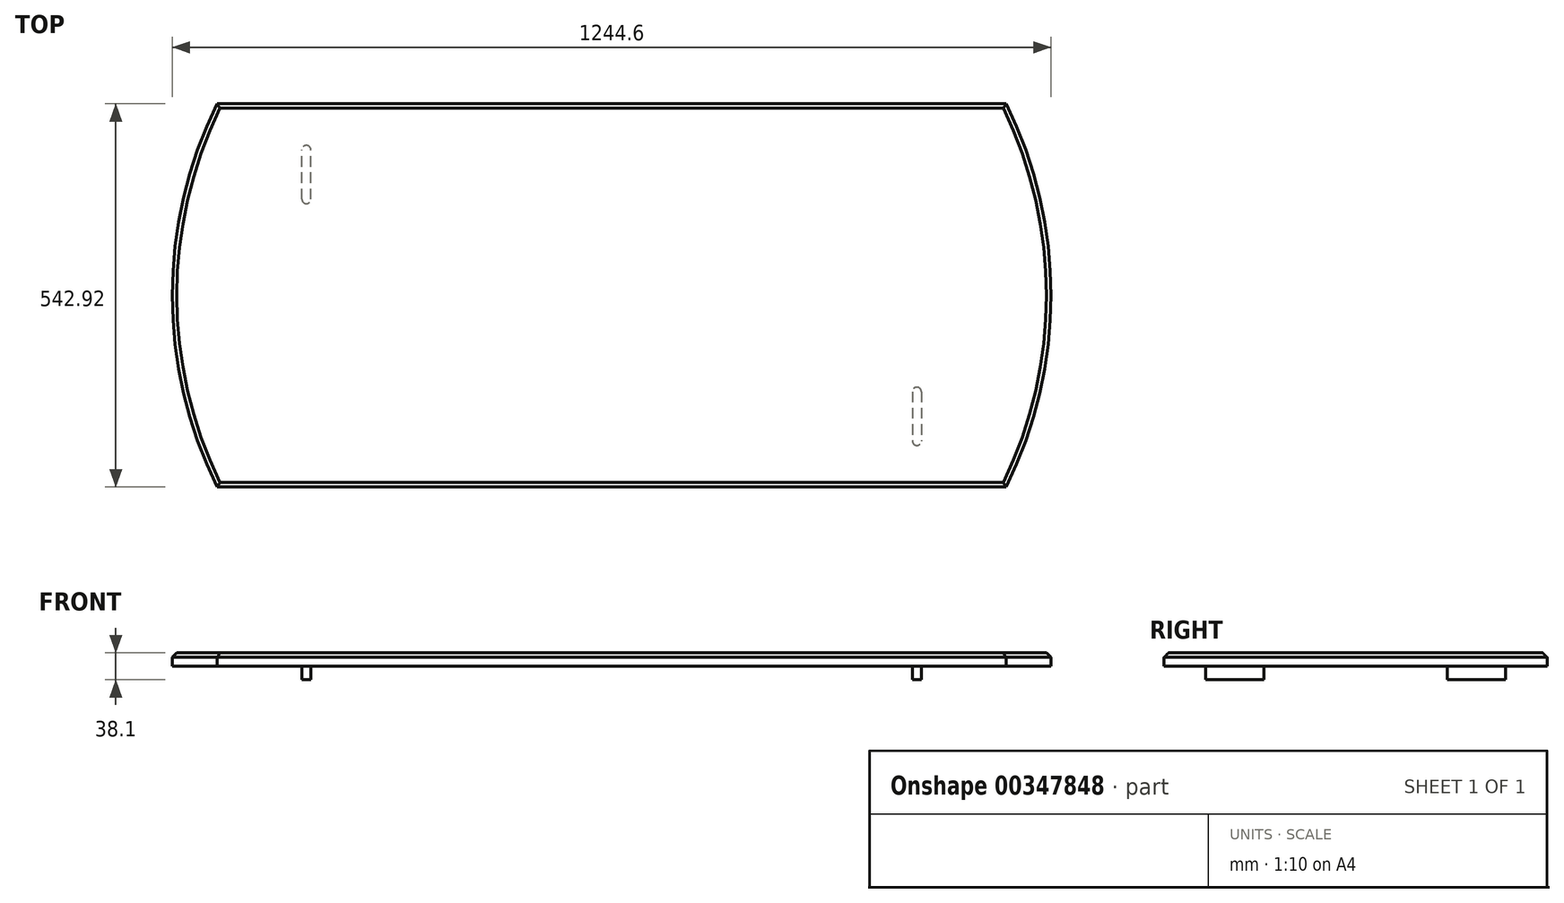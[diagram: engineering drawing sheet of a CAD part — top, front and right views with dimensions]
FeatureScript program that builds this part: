
annotation { "Feature Type Name" : "Feature", "Feature Type Description" : "" }
export const myFeature = defineFeature(function(context is Context, id is Id, definition is map)
    precondition{}
    {
        {
            var Q0;
            Q0=qCreatedBy(makeId("Front.planeOp"),FACE);
            var sketch = newSketch(context, id + "F0", { "sketchPlane" : qUnion([Q0])});
            skLineSegment(sketch, "E0.bottom", {"start": v(-622.3, -19.05) * mm, "end": v(622.3, -19.05) * mm});
            skLineSegment(sketch, "E0.top", {"start": v(-622.3, 19.05) * mm, "end": v(622.3, 19.05) * mm});
            skLineSegment(sketch, "E0.left", {"start": v(-622.3, -19.05) * mm, "end": v(-622.3, 19.05) * mm});
            skLineSegment(sketch, "E0.right", {"start": v(622.3, -19.05) * mm, "end": v(622.3, 19.05) * mm});
            skPoint(sketch, "E0.middle", {"position": v(0, 0) * mm});
            skSolve(sketch);
        }
        {
            var Q0;
            Q0=makeQuery(id+"F0.imprint","IMPRINT",FACE,{"disambiguationData":[TD([[makeQuery(id+"F0.imprint","IMPRINT",EDGE,{"derivedFrom":sQuery(id+"F0.wireOp",EDGE,"E0.bottom")}),1.0]])]});
            extrude(context, id + "F1", {"entities" : qUnion([Q0]), "endBound" : BoundingType.SYMMETRIC, "depth" : 542.92 * mm});
        }
        {
            var Q0;
            Q0=makeQuery(id+"F1.opExtrude","SWEPT_FACE",FACE,{"disambiguationData":[OSD([sQuery(id+"F0.wireOp",EDGE,"E0.top")])]});
            var sketch = newSketch(context, id + "F2", { "sketchPlane" : qUnion([Q0])});
            skLineSegment(sketch, "E1", {"start": v(-622.3, 0) * mm, "end": v(622.3, 0) * mm, "construction": true});
            skLineSegment(sketch, "E2", {"start": v(0, 271.46) * mm, "end": v(0, -271.46) * mm, "construction": true});
            skPoint(sketch, "E3", {"position": v(-558.8, 271.46) * mm});
            skPoint(sketch, "E4.MirrorP", {"position": v(-558.8, -271.46) * mm});
            skPoint(sketch, "E5.MirrorP", {"position": v(558.8, 271.46) * mm});
            skPoint(sketch, "E6.MirrorP", {"position": v(558.8, -271.46) * mm});
            skArc(sketch, "E7", {"start": v(-558.8, 271.46) * mm, "mid": v(-622.3, 0) * mm, "end": v(-558.8, -271.46) * mm});
            skArc(sketch, "E8", {"start": v(558.8, -271.46) * mm, "mid": v(622.3, 0) * mm, "end": v(558.8, 271.46) * mm});
            skSolve(sketch);
        }
        {
            var Q0;
            {var subQ0=sQuery(id+"F2.wireOp",EDGE,"E7");var subQ1=sQuery(id+"F0.wireOp",EDGE,"E0.top");var subQ2=makeQuery(id+"F1.opExtrude","CAP_EDGE",EDGE,{"disambiguationData":[OSD([subQ1])],"isStart":true});var subQ3=makeQuery(id+"F2.imprint","INTERSECT",VERTEX,{"derivedFrom":[subQ2,subQ0]});Q0=makeQuery(id+"F2.imprint","IMPRINT",FACE,{"disambiguationData":[TD([[makeQuery(id+"F2.imprint","IMPRINT",EDGE,{"disambiguationData":[TD([[subQ3,-1.0]])],"derivedFrom":subQ0}),-1.0]])]});}
            var Q1;
            {var subQ0=sQuery(id+"F2.wireOp",EDGE,"E7");var subQ1=sQuery(id+"F0.wireOp",EDGE,"E0.top");var subQ2=makeQuery(id+"F1.opExtrude","CAP_EDGE",EDGE,{"disambiguationData":[OSD([subQ1])],"isStart":false});var subQ3=makeQuery(id+"F2.imprint","INTERSECT",VERTEX,{"derivedFrom":[subQ2,subQ0]});Q1=makeQuery(id+"F2.imprint","IMPRINT",FACE,{"disambiguationData":[TD([[makeQuery(id+"F2.imprint","IMPRINT",EDGE,{"disambiguationData":[TD([[subQ3,1.0]])],"derivedFrom":subQ0}),-1.0]])]});}
            var Q2;
            {var subQ0=sQuery(id+"F2.wireOp",EDGE,"E8");var subQ1=sQuery(id+"F0.wireOp",EDGE,"E0.top");var subQ2=makeQuery(id+"F1.opExtrude","CAP_EDGE",EDGE,{"disambiguationData":[OSD([subQ1])],"isStart":true});var subQ3=makeQuery(id+"F2.imprint","INTERSECT",VERTEX,{"derivedFrom":[subQ2,subQ0]});Q2=makeQuery(id+"F2.imprint","IMPRINT",FACE,{"disambiguationData":[TD([[makeQuery(id+"F2.imprint","IMPRINT",EDGE,{"disambiguationData":[TD([[subQ3,1.0]])],"derivedFrom":subQ0}),-1.0]])]});}
            var Q3;
            {var subQ0=sQuery(id+"F2.wireOp",EDGE,"E8");var subQ1=sQuery(id+"F0.wireOp",EDGE,"E0.top");var subQ2=makeQuery(id+"F1.opExtrude","CAP_EDGE",EDGE,{"disambiguationData":[OSD([subQ1])],"isStart":false});var subQ3=makeQuery(id+"F2.imprint","INTERSECT",VERTEX,{"derivedFrom":[subQ2,subQ0]});Q3=makeQuery(id+"F2.imprint","IMPRINT",FACE,{"disambiguationData":[TD([[makeQuery(id+"F2.imprint","IMPRINT",EDGE,{"disambiguationData":[TD([[subQ3,-1.0]])],"derivedFrom":subQ0}),-1.0]])]});}
            extrude(context, id + "F3", {"entities" : qUnion([Q0, Q1, Q2, Q3]), "operationType" : NewBodyOperationType.REMOVE, "endBound" : BoundingType.THROUGH_ALL, "oppositeDirection" : true, "depth" : 25.4 * mm});
        }
        {
            var Q0;
            Q0=makeQuery(id+"F1.opExtrude","SWEPT_FACE",FACE,{"disambiguationData":[OSD([sQuery(id+"F0.wireOp",EDGE,"E0.top")])]});
            chamfer(context, id + "F4", {"entities" : qUnion([Q0]), "width" : 6.35 * mm, "tangentPropagation" : true});
        }
        {
            var Q0;
            Q0=makeQuery(id+"F1.opExtrude","SWEPT_FACE",FACE,{"disambiguationData":[OSD([sQuery(id+"F0.wireOp",EDGE,"E0.bottom")])]});
            var sketch = newSketch(context, id + "F5", { "sketchPlane" : qUnion([Q0])});
            skArc(sketch, "E9.0", {"start": v(-554.84, 265.11) * mm, "mid": v(-615.95, 0) * mm, "end": v(-554.84, -265.11) * mm});
            skLineSegment(sketch, "E9.1", {"start": v(554.84, 265.11) * mm, "end": v(-554.84, 265.11) * mm});
            skArc(sketch, "E9.2", {"start": v(554.84, -265.11) * mm, "mid": v(615.95, 0) * mm, "end": v(554.84, 265.11) * mm});
            skLineSegment(sketch, "E9.3", {"start": v(-554.84, -265.11) * mm, "end": v(554.84, -265.11) * mm});
            skSolve(sketch);
        }
        {
            var Q0;
            Q0=makeQuery(id+"F5.imprint","IMPRINT",FACE,{"disambiguationData":[TD([[makeQuery(id+"F5.imprint","IMPRINT",EDGE,{"derivedFrom":sQuery(id+"F5.wireOp",EDGE,"E9.0")}),-1.0]])]});
            extrude(context, id + "F6", {"entities" : qUnion([Q0]), "operationType" : NewBodyOperationType.REMOVE, "oppositeDirection" : true, "depth" : 19.05 * mm});
        }
        {
            var Q0;
            Q0=makeQuery(id+"F1.opExtrude","SWEPT_FACE",FACE,{"disambiguationData":[OSD([sQuery(id+"F0.wireOp",EDGE,"E0.bottom")])]});
            var sketch = newSketch(context, id + "F7", { "sketchPlane" : qUnion([Q0])});
            skLineSegment(sketch, "E10", {"start": v(-615.95, 0) * mm, "end": v(615.95, 0) * mm, "construction": true});
            skLineSegment(sketch, "E11", {"start": v(0, 265.11) * mm, "end": v(0, -265.11) * mm, "construction": true});
            skLineSegment(sketch, "E12.0", {"start": v(-615.95, 136.36) * mm, "end": v(-438.68, 136.36) * mm, "construction": true});
            skLineSegment(sketch, "E13.MirrorCS", {"start": v(-615.95, -136.36) * mm, "end": v(615.95, -136.36) * mm, "construction": true});
            skLineSegment(sketch, "E14.0", {"start": v(-425.98, 265.11) * mm, "end": v(-425.98, -265.11) * mm, "construction": true});
            skLineSegment(sketch, "E15.MirrorCS", {"start": v(425.98, 265.11) * mm, "end": v(425.98, -265.11) * mm, "construction": true});
            skLineSegment(sketch, "E16.left", {"start": v(-425.98, 136.36) * mm, "end": v(-425.98, 206.21) * mm});
            skLineSegment(sketch, "E16.right", {"start": v(-438.68, 136.36) * mm, "end": v(-438.68, 206.21) * mm});
            skArc(sketch, "E17", {"start": v(-425.98, 206.21) * mm, "mid": v(-432.33, 212.56) * mm, "end": v(-438.68, 206.21) * mm});
            skArc(sketch, "E18", {"start": v(-438.68, 136.36) * mm, "mid": v(-432.33, 130.01) * mm, "end": v(-425.98, 136.36) * mm});
            skLineSegment(sketch, "E19.trimOffspring", {"start": v(-425.98, 136.36) * mm, "end": v(615.95, 136.36) * mm, "construction": true});
            skLineSegment(sketch, "E20.MirrorCS", {"start": v(438.68, 136.36) * mm, "end": v(438.68, 206.21) * mm});
            skArc(sketch, "E21.MirrorCS", {"start": v(425.98, 206.21) * mm, "mid": v(432.33, 212.56) * mm, "end": v(438.68, 206.21) * mm});
            skArc(sketch, "E22.MirrorCS", {"start": v(438.68, 136.36) * mm, "mid": v(432.33, 130.01) * mm, "end": v(425.98, 136.36) * mm});
            skLineSegment(sketch, "E23.MirrorCS", {"start": v(425.98, 136.36) * mm, "end": v(425.98, 206.21) * mm});
            skArc(sketch, "E24.MirrorCS", {"start": v(-438.68, -136.36) * mm, "mid": v(-432.33, -130.01) * mm, "end": v(-425.98, -136.36) * mm});
            skArc(sketch, "E25.MirrorCS", {"start": v(-425.98, -206.21) * mm, "mid": v(-432.33, -212.56) * mm, "end": v(-438.68, -206.21) * mm});
            skLineSegment(sketch, "E26.MirrorCS", {"start": v(-425.98, -136.36) * mm, "end": v(-425.98, -206.21) * mm});
            skLineSegment(sketch, "E27.MirrorCS", {"start": v(-438.68, -136.36) * mm, "end": v(-438.68, -206.21) * mm});
            skLineSegment(sketch, "E28.MirrorCS", {"start": v(438.68, -136.36) * mm, "end": v(438.68, -206.21) * mm});
            skArc(sketch, "E29.MirrorCS", {"start": v(425.98, -206.21) * mm, "mid": v(432.33, -212.56) * mm, "end": v(438.68, -206.21) * mm});
            skArc(sketch, "E30.MirrorCS", {"start": v(438.68, -136.36) * mm, "mid": v(432.33, -130.01) * mm, "end": v(425.98, -136.36) * mm});
            skLineSegment(sketch, "E31.MirrorCS", {"start": v(425.98, -136.36) * mm, "end": v(425.98, -206.21) * mm});
            skSolve(sketch);
        }
        {
            var Q0;
            Q0=makeQuery(id+"F7.imprint","IMPRINT",FACE,{"disambiguationData":[TD([[makeQuery(id+"F7.imprint","IMPRINT",EDGE,{"derivedFrom":sQuery(id+"F7.wireOp",EDGE,"E16.left")}),1.0]])]});
            var Q1;
            Q1=makeQuery(id+"F7.imprint","IMPRINT",FACE,{"disambiguationData":[TD([[makeQuery(id+"F7.imprint","IMPRINT",EDGE,{"derivedFrom":sQuery(id+"F7.wireOp",EDGE,"E24.MirrorCS")}),-1.0]])]});
            var Q2;
            Q2=makeQuery(id+"F7.imprint","IMPRINT",FACE,{"disambiguationData":[TD([[makeQuery(id+"F7.imprint","IMPRINT",EDGE,{"derivedFrom":sQuery(id+"F7.wireOp",EDGE,"E29.MirrorCS")}),1.0]])]});
            var Q3;
            Q3=makeQuery(id+"F7.imprint","IMPRINT",FACE,{"disambiguationData":[TD([[makeQuery(id+"F7.imprint","IMPRINT",EDGE,{"derivedFrom":sQuery(id+"F7.wireOp",EDGE,"E21.MirrorCS")}),-1.0]])]});
            extrude(context, id + "F8", {"entities" : qUnion([Q0, Q1, Q2, Q3]), "operationType" : NewBodyOperationType.REMOVE, "depth" : -19.05 * mm});
        }
    });
